# Revit family: 500_Slenderline_Sliding_Window_XX_Standard
name_source: partatom
category: Windows
revit_build: Autodesk Revit 2014 (Build: 20130308_1515(x64)
units: mm (PartAtom-declared; Revit-internal decimal feet)

## types (33) — shared parameters
Centered In Wall = Yes
Custom Sash Width Left = 600 mm
Default Sill Height = 800 mm
Description = Slenderline Sliding Window
Equal Sash Width = Yes
Frame Thickness = 54 mm
Heavy Duty Interlocker = No
Limit Sash Height Max = 1500 mm  [stored 4.92126 ft]
Limit Sash Height Min = 300 mm  [stored 0.984252 ft]
Limit Sash Width Max = 750 mm  [stored 2.46063 ft]
Limit Sash Width Min = 300 mm  [stored 0.984252 ft]
Limit Window Height Min = 375 mm
Limit Window Width Min = 631 mm  [stored 2.07021 ft]
Manufacturer = Crealco
Model = 500
Rough Width = 3 mm  [stored 0.00984252 ft]
Sash Frame Seal = 1 mm  [stored 0.00328084 ft]
Standard Interlocker = Yes
URL = www.crealco.co.za
Wall Closure = By host
zero-valued in all types: Custom Frame Offset From Exterior, Is Heavy Duty Interlocker

## per-type parameters (varying)
| type | Area Left Sash Glazing | Area Right Sash Glazing | Clearvue SHGC Value | Clearvue U Value | Custom Windload | Custom Window Height | Custom Window Width | Energy Advantage SHGC Value | Energy Advantage U Value | Height | Intruderprufe LowE SHGC Value | Intruderprufe LowE U Value | Intruderprufe SHGC Value | Intruderprufe U Value | Limit Sash Width Left Max | Limit Sash Width Left Min | Limit Window Height Max | Limit Window Width Max | Max Pane Area | Sash Height | Sash Width Left | Sash Width Right | Width | Windload Design |
| 500SW-0906XX-1000Pa | 0.18 m² | 0.18 m² | 0.564 | 6.33 | 1000 mm  [stored 3.28084 ft] | 590 mm  [stored 1.9357 ft] | 890 mm  [stored 2.91995 ft] | 0.506 | 5.12 | 590 mm  [stored 1.9357 ft] | 0.429 | 4.81 | 0.536 | 6.2 | 559 mm  [stored 1.83399 ft] | 300 mm  [stored 0.984252 ft] | 1575 mm | 1531 mm  [stored 5.02297 ft] | 0.18 m² | 515 mm | 430 mm | 430 mm | 890 mm  [stored 2.91995 ft] | 1000 mm  [stored 3.28084 ft] |
| 500SW-1206XX-1000Pa | 0.24 m² | 0.24 m² | 0.579 | 6.3 | 1000 mm  [stored 3.28084 ft] | 590 mm  [stored 1.9357 ft] | 1190 mm  [stored 3.9042 ft] | 0.52 | 5.01 | 590 mm  [stored 1.9357 ft] | 0.44 | 4.78 | 0.55 | 6.17 | 750 mm  [stored 2.46063 ft] | 409 mm  [stored 1.34186 ft] | 1575 mm | 1531 mm  [stored 5.02297 ft] | 0.24 m² | 515 mm | 580 mm | 580 mm | 1190 mm  [stored 3.9042 ft] | 1000 mm  [stored 3.28084 ft] |
| 500SW-1506XX-1000Pa | 0.31 m² | 0.31 m² | 0.589 | 6.29 | 1000 mm  [stored 3.28084 ft] | 590 mm  [stored 1.9357 ft] | 1490 mm  [stored 4.88845 ft] | 0.528 | 4.94 | 590 mm  [stored 1.9357 ft] | 0.447 | 4.78 | 0.559 | 6.16 | 750 mm  [stored 2.46063 ft] | 709 mm  [stored 2.32612 ft] | 1575 mm | 1531 mm  [stored 5.02297 ft] | 0.31 m² | 515 mm | 730 mm | 730 mm | 1490 mm  [stored 4.88845 ft] | 1000 mm  [stored 3.28084 ft] |
| 500SW-0909XX-1000Pa | 0.3 m² | 0.3 m² | 0.632 | 6.24 | 1000 mm  [stored 3.28084 ft] | 890 mm  [stored 2.91995 ft] | 890 mm  [stored 2.91995 ft] | 0.566 | 4.57 | 890 mm  [stored 2.91995 ft] | 0.48 | 4.74 | 0.6 | 6.11 | 559 mm  [stored 1.83399 ft] | 300 mm  [stored 0.984252 ft] | 1575 mm | 1531 mm  [stored 5.02297 ft] | 0.3 m² | 815 mm | 430 mm | 430 mm | 890 mm  [stored 2.91995 ft] | 1000 mm  [stored 3.28084 ft] |
| 500SW-1209XX-1000Pa | 0.41 m² | 0.41 m² | 0.649 | 6.21 | 1000 mm  [stored 3.28084 ft] | 890 mm  [stored 2.91995 ft] | 1190 mm  [stored 3.9042 ft] | 0.82 | 4.74 | 890 mm  [stored 2.91995 ft] | 0.493 | 4.71 | 0.616 | 6.07 | 750 mm  [stored 2.46063 ft] | 409 mm  [stored 1.34186 ft] | 1575 mm | 1531 mm  [stored 5.02297 ft] | 0.41 m² | 815 mm | 580 mm | 580 mm | 1190 mm  [stored 3.9042 ft] | 1000 mm  [stored 3.28084 ft] |
| 500SW-1509XX-1000Pa | 0.52 m² | 0.52 m² | 0.66 | 6.19 | 1000 mm  [stored 3.28084 ft] | 890 mm  [stored 2.91995 ft] | 1490 mm  [stored 4.88845 ft] | 0.591 | 4.66 | 890 mm  [stored 2.91995 ft] | 0.501 | 4.7 | 0.626 | 6.06 | 750 mm  [stored 2.46063 ft] | 709 mm  [stored 2.32612 ft] | 1575 mm | 1531 mm  [stored 5.02297 ft] | 0.52 m² | 815 mm | 730 mm | 730 mm | 1490 mm  [stored 4.88845 ft] | 1000 mm  [stored 3.28084 ft] |
| 500SW-0912XX-1000Pa | 0.42 m² | 0.42 m² | 0.665 | 6.2 | 1000 mm  [stored 3.28084 ft] | 1190 mm  [stored 3.9042 ft] | 890 mm  [stored 2.91995 ft] | 0.596 | 4.75 | 1190 mm  [stored 3.9042 ft] | 0.506 | 4.7 | 0.632 | 6.06 | 559 mm  [stored 1.83399 ft] | 300 mm  [stored 0.984252 ft] | 1575 mm | 1531 mm  [stored 5.02297 ft] | 0.42 m² | 1115 mm | 430 mm | 430 mm | 890 mm  [stored 2.91995 ft] | 1000 mm  [stored 3.28084 ft] |
| 500SW-0915XX-1000Pa | 0.54 m² | 0.54 m² | 0.686 | 6.17 | 1000 mm  [stored 3.28084 ft] | 1490 mm  [stored 4.88845 ft] | 890 mm  [stored 2.91995 ft] | 0.614 | 4.67 | 1490 mm  [stored 4.88845 ft] | 0.521 | 4.67 | 0.651 | 6.03 | 559 mm  [stored 1.83399 ft] | 300 mm  [stored 0.984252 ft] | 1575 mm | 1531 mm  [stored 5.02297 ft] | 0.54 m² | 1415 mm | 430 mm | 430 mm | 890 mm  [stored 2.91995 ft] | 1000 mm  [stored 3.28084 ft] |
| 500SW-1215XX-1000Pa | 0.74 m² | 0.74 m² | 0.705 | 6.13 | 1000 mm  [stored 3.28084 ft] | 1490 mm  [stored 4.88845 ft] | 1190 mm  [stored 3.9042 ft] | 0.63 | 4.53 | 1490 mm  [stored 4.88845 ft] | 0.535 | 4.65 | 0.669 | 6 | 750 mm  [stored 2.46063 ft] | 409 mm  [stored 1.34186 ft] | 1575 mm | 1531 mm  [stored 5.02297 ft] | 0.74 m² | 1415 mm | 580 mm | 580 mm | 1190 mm  [stored 3.9042 ft] | 1000 mm  [stored 3.28084 ft] |
| 500SW-1515XX-1000Pa | 0.94 m² | 0.94 m² | 0.716 | 6.11 | 1000 mm  [stored 3.28084 ft] | 1490 mm  [stored 4.88845 ft] | 1490 mm  [stored 4.88845 ft] | 0.64 | 4.44 | 1490 mm  [stored 4.88845 ft] | 0.543 | 4.63 | 0.679 | 5.97 | 750 mm  [stored 2.46063 ft] | 709 mm  [stored 2.32612 ft] | 1575 mm | 1531 mm  [stored 5.02297 ft] | 0.94 m² | 1415 mm | 730 mm | 730 mm | 1490 mm  [stored 4.88845 ft] | 1000 mm  [stored 3.28084 ft] |
| 500SW-1212XX-1000Pa | 0.57 m² | 0.57 m² | 0.684 | 6.16 | 1000 mm  [stored 3.28084 ft] | 1190 mm  [stored 3.9042 ft] | 1190 mm  [stored 3.9042 ft] | 0.612 | 4.61 | 1190 mm  [stored 3.9042 ft] | 0.519 | 4.67 | 0.649 | 6.03 | 750 mm  [stored 2.46063 ft] | 409 mm  [stored 1.34186 ft] | 1575 mm | 1531 mm  [stored 5.02297 ft] | 0.57 m² | 1115 mm | 580 mm | 580 mm | 1190 mm  [stored 3.9042 ft] | 1000 mm  [stored 3.28084 ft] |
| 500SW-1512XX-1000Pa | 0.73 m² | 0.73 m² | 0.695 | 6.14 | 1000 mm  [stored 3.28084 ft] | 1190 mm  [stored 3.9042 ft] | 1490 mm  [stored 4.88845 ft] | 0.622 | 4.52 | 1190 mm  [stored 3.9042 ft] | 0.527 | 4.65 | 0.659 | 6 | 750 mm  [stored 2.46063 ft] | 709 mm  [stored 2.32612 ft] | 1575 mm | 1531 mm  [stored 5.02297 ft] | 0.73 m² | 1115 mm | 730 mm | 730 mm | 1490 mm  [stored 4.88845 ft] | 1000 mm  [stored 3.28084 ft] |
| 500SW-0906XX-1500Pa | 0.18 m² | 0.18 m² | 0.564 | 6.33 | 1500 mm  [stored 4.92126 ft] | 590 mm  [stored 1.9357 ft] | 890 mm  [stored 2.91995 ft] | 0.506 | 5.12 | 590 mm  [stored 1.9357 ft] | 0.429 | 4.81 | 0.536 | 6.2 | 559 mm  [stored 1.83399 ft] | 300 mm  [stored 0.984252 ft] | 1575 mm | 1531 mm  [stored 5.02297 ft] | 0.18 m² | 515 mm | 430 mm | 430 mm | 890 mm  [stored 2.91995 ft] | 1500 mm  [stored 4.92126 ft] |
| 500SW-0906XX-2000Pa | 0.18 m² | 0.18 m² | 0.564 | 6.33 | 2000 mm  [stored 6.56168 ft] | 590 mm  [stored 1.9357 ft] | 890 mm  [stored 2.91995 ft] | 0.506 | 5.12 | 590 mm  [stored 1.9357 ft] | 0.429 | 4.81 | 0.536 | 6.2 | 559 mm  [stored 1.83399 ft] | 300 mm  [stored 0.984252 ft] | 1575 mm | 1531 mm  [stored 5.02297 ft] | 0.18 m² | 515 mm | 430 mm | 430 mm | 890 mm  [stored 2.91995 ft] | 2000 mm  [stored 6.56168 ft] |
| 500SW-0909XX-1500Pa | 0.3 m² | 0.3 m² | 0.632 | 6.24 | 1500 mm  [stored 4.92126 ft] | 890 mm  [stored 2.91995 ft] | 890 mm  [stored 2.91995 ft] | 0.566 | 4.57 | 890 mm  [stored 2.91995 ft] | 0.48 | 4.74 | 0.6 | 6.11 | 559 mm  [stored 1.83399 ft] | 300 mm  [stored 0.984252 ft] | 1575 mm | 1531 mm  [stored 5.02297 ft] | 0.3 m² | 815 mm | 430 mm | 430 mm | 890 mm  [stored 2.91995 ft] | 1500 mm  [stored 4.92126 ft] |
| 500SW-0909XX-2000Pa | 0.3 m² | 0.3 m² | 0.632 | 6.24 | 2000 mm  [stored 6.56168 ft] | 890 mm  [stored 2.91995 ft] | 890 mm  [stored 2.91995 ft] | 0.566 | 4.57 | 890 mm  [stored 2.91995 ft] | 0.48 | 4.74 | 0.6 | 6.11 | 559 mm  [stored 1.83399 ft] | 300 mm  [stored 0.984252 ft] | 1575 mm | 1531 mm  [stored 5.02297 ft] | 0.3 m² | 815 mm | 430 mm | 430 mm | 890 mm  [stored 2.91995 ft] | 2000 mm  [stored 6.56168 ft] |
| 500SW-0912XX-1500Pa | 0.42 m² | 0.42 m² | 0.665 | 6.2 | 1500 mm  [stored 4.92126 ft] | 1190 mm  [stored 3.9042 ft] | 890 mm  [stored 2.91995 ft] | 0.596 | 4.75 | 1190 mm  [stored 3.9042 ft] | 0.506 | 4.7 | 0.632 | 6.06 | 559 mm  [stored 1.83399 ft] | 300 mm  [stored 0.984252 ft] | 1575 mm | 1531 mm  [stored 5.02297 ft] | 0.42 m² | 1115 mm | 430 mm | 430 mm | 890 mm  [stored 2.91995 ft] | 1500 mm  [stored 4.92126 ft] |
| 500SW-0912XX-2000Pa | 0.42 m² | 0.42 m² | 0.665 | 6.2 | 2000 mm  [stored 6.56168 ft] | 1190 mm  [stored 3.9042 ft] | 890 mm  [stored 2.91995 ft] | 0.596 | 4.75 | 1190 mm  [stored 3.9042 ft] | 0.506 | 4.7 | 0.632 | 6.06 | 559 mm  [stored 1.83399 ft] | 300 mm  [stored 0.984252 ft] | 1575 mm | 1531 mm  [stored 5.02297 ft] | 0.42 m² | 1115 mm | 430 mm | 430 mm | 890 mm  [stored 2.91995 ft] | 2000 mm  [stored 6.56168 ft] |
| 500SW-0915XX-1500Pa | 0.54 m² | 0.54 m² | 0.686 | 6.17 | 1500 mm  [stored 4.92126 ft] | 1490 mm  [stored 4.88845 ft] | 890 mm  [stored 2.91995 ft] | 0.614 | 4.67 | 1490 mm  [stored 4.88845 ft] | 0.521 | 4.67 | 0.651 | 6.03 | 559 mm  [stored 1.83399 ft] | 300 mm  [stored 0.984252 ft] | 1575 mm | 1531 mm  [stored 5.02297 ft] | 0.54 m² | 1415 mm | 430 mm | 430 mm | 890 mm  [stored 2.91995 ft] | 1500 mm  [stored 4.92126 ft] |
| 500SW-0915XX-2000Pa | 0.54 m² | 0.54 m² | 0.686 | 6.17 | 2000 mm  [stored 6.56168 ft] | 1490 mm  [stored 4.88845 ft] | 890 mm  [stored 2.91995 ft] | 0.614 | 4.67 | 1490 mm  [stored 4.88845 ft] | 0.521 | 4.67 | 0.651 | 6.03 | 559 mm  [stored 1.83399 ft] | 300 mm  [stored 0.984252 ft] | 1575 mm | 1531 mm  [stored 5.02297 ft] | 0.54 m² | 1415 mm | 430 mm | 430 mm | 890 mm  [stored 2.91995 ft] | 2000 mm  [stored 6.56168 ft] |
| 500SW-1206XX-1500Pa | 0.24 m² | 0.24 m² | 0.579 | 6.3 | 1500 mm  [stored 4.92126 ft] | 590 mm  [stored 1.9357 ft] | 1190 mm  [stored 3.9042 ft] | 0.52 | 5.01 | 590 mm  [stored 1.9357 ft] | 0.44 | 4.78 | 0.55 | 6.17 | 750 mm  [stored 2.46063 ft] | 409 mm  [stored 1.34186 ft] | 1575 mm | 1531 mm  [stored 5.02297 ft] | 0.24 m² | 515 mm | 580 mm | 580 mm | 1190 mm  [stored 3.9042 ft] | 1500 mm  [stored 4.92126 ft] |
| 500SW-1206XX-2000Pa | 0.24 m² | 0.24 m² | 0.579 | 6.3 | 2000 mm  [stored 6.56168 ft] | 590 mm  [stored 1.9357 ft] | 1190 mm  [stored 3.9042 ft] | 0.52 | 5.01 | 590 mm  [stored 1.9357 ft] | 0.44 | 4.78 | 0.55 | 6.17 | 750 mm  [stored 2.46063 ft] | 409 mm  [stored 1.34186 ft] | 1575 mm | 1531 mm  [stored 5.02297 ft] | 0.24 m² | 515 mm | 580 mm | 580 mm | 1190 mm  [stored 3.9042 ft] | 2000 mm  [stored 6.56168 ft] |
| 500SW-1209XX-1500Pa | 0.41 m² | 0.41 m² | 0.649 | 6.21 | 1500 mm  [stored 4.92126 ft] | 890 mm  [stored 2.91995 ft] | 1190 mm  [stored 3.9042 ft] | 0.82 | 4.74 | 890 mm  [stored 2.91995 ft] | 0.493 | 4.71 | 0.616 | 6.07 | 750 mm  [stored 2.46063 ft] | 409 mm  [stored 1.34186 ft] | 1575 mm | 1531 mm  [stored 5.02297 ft] | 0.41 m² | 815 mm | 580 mm | 580 mm | 1190 mm  [stored 3.9042 ft] | 1500 mm  [stored 4.92126 ft] |
| 500SW-1209XX-2000Pa | 0.41 m² | 0.41 m² | 0.649 | 6.21 | 2000 mm  [stored 6.56168 ft] | 890 mm  [stored 2.91995 ft] | 1190 mm  [stored 3.9042 ft] | 0.82 | 4.74 | 890 mm  [stored 2.91995 ft] | 0.493 | 4.71 | 0.616 | 6.07 | 750 mm  [stored 2.46063 ft] | 409 mm  [stored 1.34186 ft] | 1575 mm | 1531 mm  [stored 5.02297 ft] | 0.41 m² | 815 mm | 580 mm | 580 mm | 1190 mm  [stored 3.9042 ft] | 2000 mm  [stored 6.56168 ft] |
| 500SW-1212XX-1500Pa | 0.57 m² | 0.57 m² | 0.684 | 6.16 | 1500 mm  [stored 4.92126 ft] | 1190 mm  [stored 3.9042 ft] | 1190 mm  [stored 3.9042 ft] | 0.612 | 4.61 | 1190 mm  [stored 3.9042 ft] | 0.519 | 4.67 | 0.649 | 6.03 | 750 mm  [stored 2.46063 ft] | 409 mm  [stored 1.34186 ft] | 1575 mm | 1531 mm  [stored 5.02297 ft] | 0.57 m² | 1115 mm | 580 mm | 580 mm | 1190 mm  [stored 3.9042 ft] | 1500 mm  [stored 4.92126 ft] |
| 500SW-1212XX-2000Pa | 0.57 m² | 0.57 m² | 0.684 | 6.16 | 2000 mm  [stored 6.56168 ft] | 1190 mm  [stored 3.9042 ft] | 1190 mm  [stored 3.9042 ft] | 0.612 | 4.61 | 1190 mm  [stored 3.9042 ft] | 0.519 | 4.67 | 0.649 | 6.03 | 750 mm  [stored 2.46063 ft] | 409 mm  [stored 1.34186 ft] | 1575 mm | 1531 mm  [stored 5.02297 ft] | 0.57 m² | 1115 mm | 580 mm | 580 mm | 1190 mm  [stored 3.9042 ft] | 2000 mm  [stored 6.56168 ft] |
| 500SW-1215XX-1500Pa | 0.74 m² | 0.74 m² | 0.705 | 6.13 | 1500 mm  [stored 4.92126 ft] | 1490 mm  [stored 4.88845 ft] | 1190 mm  [stored 3.9042 ft] | 0.63 | 4.53 | 1490 mm  [stored 4.88845 ft] | 0.535 | 4.65 | 0.669 | 6 | 750 mm  [stored 2.46063 ft] | 409 mm  [stored 1.34186 ft] | 1575 mm | 1531 mm  [stored 5.02297 ft] | 0.74 m² | 1415 mm | 580 mm | 580 mm | 1190 mm  [stored 3.9042 ft] | 1500 mm  [stored 4.92126 ft] |
| 500SW-1215XX-2000Pa | 0.42 m² | 0.42 m² | 0.705 | 6.13 | 2000 mm  [stored 6.56168 ft] | 1490 mm  [stored 4.88845 ft] | 1190 mm  [stored 3.9042 ft] | 0.63 | 4.53 | 1190 mm  [stored 3.9042 ft] | 0.535 | 4.65 | 0.669 | 6 | 559 mm  [stored 1.83399 ft] | 300 mm  [stored 0.984252 ft] | 1190 mm  [stored 3.9042 ft] | 890 mm  [stored 2.91995 ft] | 0.42 m² | 1115 mm | 430 mm | 430 mm | 890 mm  [stored 2.91995 ft] | 2000 mm  [stored 6.56168 ft] |
| 500SW-1506XX-1500Pa | 0.31 m² | 0.31 m² | 0.589 | 6.29 | 1500 mm  [stored 4.92126 ft] | 590 mm  [stored 1.9357 ft] | 1490 mm  [stored 4.88845 ft] | 0.528 | 4.94 | 590 mm  [stored 1.9357 ft] | 0.447 | 4.78 | 0.559 | 6.16 | 750 mm  [stored 2.46063 ft] | 709 mm  [stored 2.32612 ft] | 1575 mm | 1531 mm  [stored 5.02297 ft] | 0.31 m² | 515 mm | 730 mm | 730 mm | 1490 mm  [stored 4.88845 ft] | 1500 mm  [stored 4.92126 ft] |
| 500SW-1506XX-2000Pa | 0.31 m² | 0.31 m² | 0.589 | 6.29 | 2000 mm  [stored 6.56168 ft] | 590 mm  [stored 1.9357 ft] | 1490 mm  [stored 4.88845 ft] | 0.528 | 4.94 | 590 mm  [stored 1.9357 ft] | 0.447 | 4.78 | 0.559 | 6.16 | 750 mm  [stored 2.46063 ft] | 709 mm  [stored 2.32612 ft] | 1575 mm | 1531 mm  [stored 5.02297 ft] | 0.31 m² | 515 mm | 730 mm | 730 mm | 1490 mm  [stored 4.88845 ft] | 2000 mm  [stored 6.56168 ft] |
| 500SW-1509XX-1500Pa | 0.52 m² | 0.52 m² | 0.66 | 6.19 | 1500 mm  [stored 4.92126 ft] | 890 mm  [stored 2.91995 ft] | 1490 mm  [stored 4.88845 ft] | 0.591 | 4.66 | 890 mm  [stored 2.91995 ft] | 0.501 | 4.7 | 0.626 | 6.06 | 750 mm  [stored 2.46063 ft] | 709 mm  [stored 2.32612 ft] | 1575 mm | 1531 mm  [stored 5.02297 ft] | 0.52 m² | 815 mm | 730 mm | 730 mm | 1490 mm  [stored 4.88845 ft] | 1500 mm  [stored 4.92126 ft] |
| 500SW-1509XX-2000Pa | 0.52 m² | 0.52 m² | 0.66 | 6.19 | 2000 mm  [stored 6.56168 ft] | 890 mm  [stored 2.91995 ft] | 1490 mm  [stored 4.88845 ft] | 0.591 | 4.66 | 890 mm  [stored 2.91995 ft] | 0.501 | 4.7 | 0.626 | 6.06 | 750 mm  [stored 2.46063 ft] | 709 mm  [stored 2.32612 ft] | 1575 mm | 1531 mm  [stored 5.02297 ft] | 0.52 m² | 815 mm | 730 mm | 730 mm | 1490 mm  [stored 4.88845 ft] | 2000 mm  [stored 6.56168 ft] |
| 500SW-1512XX-1500Pa | 0.73 m² | 0.73 m² | 0.695 | 6.14 | 1500 mm  [stored 4.92126 ft] | 1190 mm  [stored 3.9042 ft] | 1490 mm  [stored 4.88845 ft] | 0.622 | 4.52 | 1190 mm  [stored 3.9042 ft] | 0.527 | 4.65 | 0.659 | 6 | 750 mm  [stored 2.46063 ft] | 709 mm  [stored 2.32612 ft] | 1575 mm | 1531 mm  [stored 5.02297 ft] | 0.73 m² | 1115 mm | 730 mm | 730 mm | 1490 mm  [stored 4.88845 ft] | 1500 mm  [stored 4.92126 ft] |

note: [stored X ft] marks values corroborated as IEEE doubles in the binary element streams (Revit-internal decimal feet)

## geometry (parser evidence)
native form markers: Sweep x32
no freeform markers — native parametric forms only
